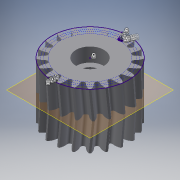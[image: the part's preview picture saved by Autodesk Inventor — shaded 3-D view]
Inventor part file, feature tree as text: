
AUTODESK INVENTOR PART (.ipt)
format: ipt  version: 2017 (Build 210142000, 142)  size: 882,688 bytes
history: native  units: mm
features: sketch x4, extrude x4, pattern_circular x2, helix x2, plane x1, mirror x1, projected_geometry x1
ambient origin geometry x8: Origin, YZ Plane, XZ Plane, XY Plane, X Axis, Y Axis, Z Axis, Center Point
bodies: Solid1 (feature_tree)
feature tree (15):
  sketch  "Sketch1"  dims[d0=20.0mm d1=0.0mm]
  extrude  "Extrusion1"  TaperAngle=0.0deg  [1 undecoded]
  extrude  "Extrusion2"  Depth=200.0mm TaperAngle=360.0deg
  pattern_circular  "Circular Pattern1"  [2 undecoded]
  extrude  "Extrusion3"  Depth=5.0mm TaperAngle=0.0deg
  extrude  "Extrusion4"  Depth=200.0mm TaperAngle=360.0deg
  plane  "Work Plane1"
  mirror  "Mirror1"
  helix  "Coil1"  [1 undecoded]
  helix  "Coil2"  [1 undecoded]
  pattern_circular  "Circular Pattern2"  [2 undecoded]
  sketch  "Sketch2"  dims[d2=10.0mm d3=0.0mm d4=200.0mm d5=360.0deg]
  sketch  "Sketch3"  dims[d7=10.0mm]
  sketch  "Sketch4"  dims[d8=5.0mm d9=0.0mm d10=6.0mm d11=5.0mm d12=0.0mm d13=10.0mm d14=10.0mm d15=0.1mm d16=0.0mm d17=90.0deg d18=90.0deg d19=0.0mm d20=0.0mm d21=10.0mm d22=10.0mm d23=0.1mm d24=0.0mm d25=90.0deg d26=90.0deg d27=0.0mm d28=0.0mm d29=200.0mm d30=360.0deg]
  projected_geometry  "Projected Loop1"
note: 7 required parameter values undecoded (feature->parameter linkage not recoverable at this tier; creation-order binding heuristic only, values carry confidence <= 0.55)
